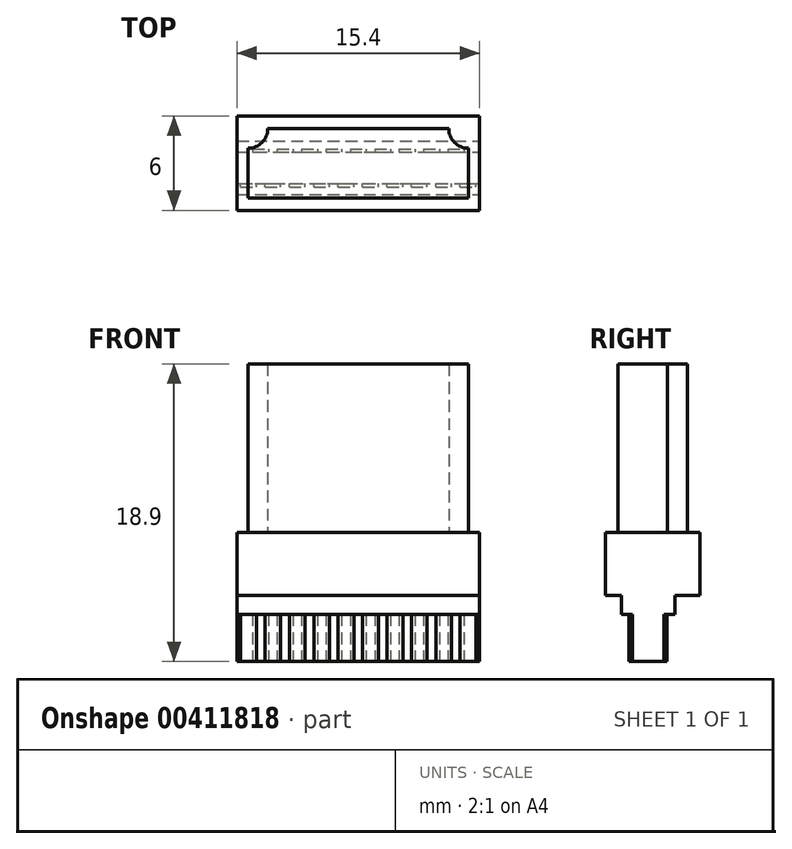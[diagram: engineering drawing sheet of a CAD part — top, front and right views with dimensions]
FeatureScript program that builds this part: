
annotation { "Feature Type Name" : "Feature", "Feature Type Description" : "" }
export const myFeature = defineFeature(function(context is Context, id is Id, definition is map)
    precondition{}
    {
        {
            var Q0;
            Q0=qCreatedBy(makeId("Top.planeOp"),FACE);
            var sketch = newSketch(context, id + "F0", { "sketchPlane" : qUnion([Q0])});
            skLineSegment(sketch, "E0.bottom", {"start": v(0, 0) * mm, "end": v(14, 0) * mm});
            skLineSegment(sketch, "E0.top", {"start": v(1.25, 4.4) * mm, "end": v(12.75, 4.4) * mm});
            skLineSegment(sketch, "E0.left", {"start": v(0, 0) * mm, "end": v(0, 3.15) * mm});
            skLineSegment(sketch, "E0.right", {"start": v(14, 0) * mm, "end": v(14, 3.15) * mm});
            skArc(sketch, "E1", {"start": v(0, 3.15) * mm, "mid": v(0.88, 3.52) * mm, "end": v(1.25, 4.4) * mm});
            skArc(sketch, "E2", {"start": v(12.75, 4.4) * mm, "mid": v(13.12, 3.52) * mm, "end": v(14, 3.15) * mm});
            skSolve(sketch);
        }
        {
            var Q0;
            Q0=makeQuery(id+"F0.imprint","IMPRINT",FACE,{"disambiguationData":[TD([[makeQuery(id+"F0.imprint","IMPRINT",EDGE,{"derivedFrom":sQuery(id+"F0.wireOp",EDGE,"E0.bottom")}),1.0]])]});
            extrude(context, id + "F1", {"entities" : qUnion([Q0]), "depth" : 10.7 * mm});
        }
        {
            var Q0;
            Q0=makeQuery(id+"F1.opExtrude","CAP_FACE",FACE,{"disambiguationData":[OSD([sQuery(id+"F0.wireOp",EDGE,"E0.bottom"),sQuery(id+"F0.wireOp",EDGE,"E0.top"),sQuery(id+"F0.wireOp",EDGE,"E0.left"),sQuery(id+"F0.wireOp",EDGE,"E0.right"),sQuery(id+"F0.wireOp",EDGE,"E1"),sQuery(id+"F0.wireOp",EDGE,"E2")])],"isStart":true});
            var sketch = newSketch(context, id + "F2", { "sketchPlane" : qUnion([Q0])});
            skLineSegment(sketch, "E3.bottom", {"start": v(-0.7, 0.8) * mm, "end": v(14.7, 0.8) * mm});
            skLineSegment(sketch, "E3.top", {"start": v(-0.7, -5.2) * mm, "end": v(14.7, -5.2) * mm});
            skLineSegment(sketch, "E3.left", {"start": v(-0.7, 0.8) * mm, "end": v(-0.7, -5.2) * mm});
            skLineSegment(sketch, "E3.right", {"start": v(14.7, 0.8) * mm, "end": v(14.7, -5.2) * mm});
            skSolve(sketch);
        }
        {
            var Q0;
            Q0=makeQuery(id+"F2.imprint","IMPRINT",FACE,{"disambiguationData":[TD([[makeQuery(id+"F2.imprint","IMPRINT",EDGE,{"derivedFrom":sQuery(id+"F2.wireOp",EDGE,"E3.bottom")}),-1.0]])]});
            var Q1;
            Q1=makeQuery(id+"F2.imprint","IMPRINT",FACE,{"disambiguationData":[TD([[makeQuery(id+"F2.imprint","IMPRINT",EDGE,{"derivedFrom":makeQuery(id+"F1.opExtrude","CAP_EDGE",EDGE,{"disambiguationData":[OSD([sQuery(id+"F0.wireOp",EDGE,"E0.bottom")])],"isStart":true})}),-1.0]])]});
            extrude(context, id + "F3", {"entities" : qUnion([Q0, Q1]), "depth" : 4 * mm});
        }
        {
            var Q0;
            Q0=makeQuery(id+"F3.opExtrude","CAP_FACE",FACE,{"disambiguationData":[OSD([sQuery(id+"F2.wireOp",EDGE,"E3.bottom"),sQuery(id+"F2.wireOp",EDGE,"E3.top"),sQuery(id+"F2.wireOp",EDGE,"E3.left"),sQuery(id+"F2.wireOp",EDGE,"E3.right")])],"isStart":false});
            var sketch = newSketch(context, id + "F4", { "sketchPlane" : qUnion([Q0])});
            skLineSegment(sketch, "E4.bottom", {"start": v(-0.7, -0.2) * mm, "end": v(14.7, -0.2) * mm});
            skLineSegment(sketch, "E4.top", {"start": v(-0.7, -3.6) * mm, "end": v(14.7, -3.6) * mm});
            skLineSegment(sketch, "E4.left", {"start": v(-0.7, -0.2) * mm, "end": v(-0.7, -3.6) * mm});
            skLineSegment(sketch, "E4.right", {"start": v(14.7, -0.2) * mm, "end": v(14.7, -3.6) * mm});
            skSolve(sketch);
        }
        {
            var Q0;
            Q0=makeQuery(id+"F4.imprint","IMPRINT",FACE,{"disambiguationData":[TD([[makeQuery(id+"F4.imprint","IMPRINT",EDGE,{"derivedFrom":sQuery(id+"F4.wireOp",EDGE,"E4.bottom")}),-1.0]])]});
            extrude(context, id + "F5", {"entities" : qUnion([Q0]), "operationType" : NewBodyOperationType.ADD, "depth" : 1.2 * mm});
        }
        {
            var Q0;
            Q0=makeQuery(id+"F5.opExtrude","CAP_FACE",FACE,{"disambiguationData":[OSD([sQuery(id+"F4.wireOp",EDGE,"E4.bottom"),sQuery(id+"F4.wireOp",EDGE,"E4.top"),sQuery(id+"F4.wireOp",EDGE,"E4.left"),sQuery(id+"F4.wireOp",EDGE,"E4.right")])],"isStart":false});
            var sketch = newSketch(context, id + "F6", { "sketchPlane" : qUnion([Q0])});
            skLineSegment(sketch, "E5.bottom", {"start": v(-0.7, -0.9) * mm, "end": v(14.7, -0.9) * mm});
            skLineSegment(sketch, "E5.top", {"start": v(-0.7, -2.9) * mm, "end": v(14.7, -2.9) * mm});
            skLineSegment(sketch, "E5.left", {"start": v(-0.7, -0.9) * mm, "end": v(-0.7, -2.9) * mm});
            skLineSegment(sketch, "E5.right", {"start": v(14.7, -0.9) * mm, "end": v(14.7, -2.9) * mm});
            skSolve(sketch);
        }
        {
            var Q0;
            Q0=makeQuery(id+"F6.imprint","IMPRINT",FACE,{"disambiguationData":[TD([[makeQuery(id+"F6.imprint","IMPRINT",EDGE,{"derivedFrom":sQuery(id+"F6.wireOp",EDGE,"E5.bottom")}),-1.0]])]});
            extrude(context, id + "F7", {"entities" : qUnion([Q0]), "operationType" : NewBodyOperationType.ADD, "depth" : 3 * mm});
        }
        {
            var Q0;
            Q0=makeQuery(id+"F7.opExtrude","SWEPT_FACE",FACE,{"disambiguationData":[OSD([sQuery(id+"F6.wireOp",EDGE,"E5.bottom")])]});
            var sketch = newSketch(context, id + "F8", { "sketchPlane" : qUnion([Q0])});
            skLineSegment(sketch, "E6.bottom", {"start": v(-0.47, -5.2) * mm, "end": v(0.52, -5.2) * mm});
            skLineSegment(sketch, "E6.top", {"start": v(-0.47, -8.2) * mm, "end": v(0.53, -8.2) * mm});
            skLineSegment(sketch, "E6.left", {"start": v(-0.48, -5.2) * mm, "end": v(-0.47, -8.2) * mm});
            skLineSegment(sketch, "E6.right", {"start": v(0.52, -5.2) * mm, "end": v(0.53, -8.2) * mm});
            skLineSegment(sketch, "E7.1.0.0", {"start": v(1.08, -5.2) * mm, "end": v(2.07, -5.2) * mm});
            skLineSegment(sketch, "E7.1.0.1", {"start": v(1.07, -5.2) * mm, "end": v(1.08, -8.2) * mm});
            skLineSegment(sketch, "E7.1.0.2", {"start": v(2.08, -5.2) * mm, "end": v(2.08, -8.2) * mm});
            skLineSegment(sketch, "E7.1.0.3", {"start": v(1.08, -8.2) * mm, "end": v(2.08, -8.2) * mm});
            skLineSegment(sketch, "E7.2.0.0", {"start": v(2.63, -5.2) * mm, "end": v(3.62, -5.2) * mm});
            skLineSegment(sketch, "E7.2.0.1", {"start": v(2.62, -5.2) * mm, "end": v(2.62, -8.2) * mm});
            skLineSegment(sketch, "E7.2.0.2", {"start": v(3.62, -5.2) * mm, "end": v(3.62, -8.2) * mm});
            skLineSegment(sketch, "E7.2.0.3", {"start": v(2.63, -8.2) * mm, "end": v(3.62, -8.2) * mm});
            skLineSegment(sketch, "E7.3.0.0", {"start": v(4.18, -5.2) * mm, "end": v(5.17, -5.2) * mm});
            skLineSegment(sketch, "E7.3.0.1", {"start": v(4.18, -5.2) * mm, "end": v(4.18, -8.2) * mm});
            skLineSegment(sketch, "E7.3.0.2", {"start": v(5.17, -5.2) * mm, "end": v(5.17, -8.2) * mm});
            skLineSegment(sketch, "E7.3.0.3", {"start": v(4.18, -8.2) * mm, "end": v(5.18, -8.2) * mm});
            skLineSegment(sketch, "E7.4.0.0", {"start": v(5.73, -5.2) * mm, "end": v(6.72, -5.2) * mm});
            skLineSegment(sketch, "E7.4.0.1", {"start": v(5.73, -5.2) * mm, "end": v(5.73, -8.2) * mm});
            skLineSegment(sketch, "E7.4.0.2", {"start": v(6.72, -5.2) * mm, "end": v(6.72, -8.2) * mm});
            skLineSegment(sketch, "E7.4.0.3", {"start": v(5.73, -8.2) * mm, "end": v(6.73, -8.2) * mm});
            skLineSegment(sketch, "E7.5.0.0", {"start": v(7.28, -5.2) * mm, "end": v(8.28, -5.2) * mm});
            skLineSegment(sketch, "E7.5.0.1", {"start": v(7.28, -5.2) * mm, "end": v(7.28, -8.2) * mm});
            skLineSegment(sketch, "E7.5.0.2", {"start": v(8.28, -5.2) * mm, "end": v(8.28, -8.2) * mm});
            skLineSegment(sketch, "E7.5.0.3", {"start": v(7.28, -8.2) * mm, "end": v(8.28, -8.2) * mm});
            skLineSegment(sketch, "E7.6.0.0", {"start": v(8.83, -5.2) * mm, "end": v(9.83, -5.2) * mm});
            skLineSegment(sketch, "E7.6.0.1", {"start": v(8.83, -5.2) * mm, "end": v(8.83, -8.2) * mm});
            skLineSegment(sketch, "E7.6.0.2", {"start": v(9.83, -5.2) * mm, "end": v(9.83, -8.2) * mm});
            skLineSegment(sketch, "E7.6.0.3", {"start": v(8.83, -8.2) * mm, "end": v(9.83, -8.2) * mm});
            skLineSegment(sketch, "E7.7.0.0", {"start": v(10.38, -5.2) * mm, "end": v(11.38, -5.2) * mm});
            skLineSegment(sketch, "E7.7.0.1", {"start": v(10.38, -5.2) * mm, "end": v(10.38, -8.2) * mm});
            skLineSegment(sketch, "E7.7.0.2", {"start": v(11.38, -5.2) * mm, "end": v(11.38, -8.2) * mm});
            skLineSegment(sketch, "E7.7.0.3", {"start": v(10.38, -8.2) * mm, "end": v(11.38, -8.2) * mm});
            skLineSegment(sketch, "E7.8.0.0", {"start": v(11.93, -5.2) * mm, "end": v(12.93, -5.2) * mm});
            skLineSegment(sketch, "E7.8.0.1", {"start": v(11.93, -5.2) * mm, "end": v(11.93, -8.2) * mm});
            skLineSegment(sketch, "E7.8.0.2", {"start": v(12.93, -5.2) * mm, "end": v(12.93, -8.2) * mm});
            skLineSegment(sketch, "E7.8.0.3", {"start": v(11.93, -8.2) * mm, "end": v(12.93, -8.2) * mm});
            skLineSegment(sketch, "E7.9.0.0", {"start": v(13.48, -5.2) * mm, "end": v(14.47, -5.2) * mm});
            skLineSegment(sketch, "E7.9.0.1", {"start": v(13.48, -5.2) * mm, "end": v(13.48, -8.2) * mm});
            skLineSegment(sketch, "E7.9.0.2", {"start": v(14.47, -5.2) * mm, "end": v(14.47, -8.2) * mm});
            skLineSegment(sketch, "E7.9.0.3", {"start": v(13.48, -8.2) * mm, "end": v(14.47, -8.2) * mm});
            skLineSegment(sketch, "E7.direction1", {"start": v(-0.47, -5.2) * mm, "end": v(1.08, -5.2) * mm, "construction": true});
            skSolve(sketch);
        }
        {
            var Q0;
            Q0=makeQuery(id+"F8.imprint","IMPRINT",FACE,{"disambiguationData":[TD([[makeQuery(id+"F8.imprint","IMPRINT",EDGE,{"derivedFrom":sQuery(id+"F8.wireOp",EDGE,"E6.bottom")}),-1.0]])]});
            var Q1;
            Q1=makeQuery(id+"F8.imprint","IMPRINT",FACE,{"disambiguationData":[TD([[makeQuery(id+"F8.imprint","IMPRINT",EDGE,{"derivedFrom":sQuery(id+"F8.wireOp",EDGE,"E7.1.0.0")}),-1.0]])]});
            var Q2;
            Q2=makeQuery(id+"F8.imprint","IMPRINT",FACE,{"disambiguationData":[TD([[makeQuery(id+"F8.imprint","IMPRINT",EDGE,{"derivedFrom":sQuery(id+"F8.wireOp",EDGE,"E7.2.0.0")}),-1.0]])]});
            var Q3;
            Q3=makeQuery(id+"F8.imprint","IMPRINT",FACE,{"disambiguationData":[TD([[makeQuery(id+"F8.imprint","IMPRINT",EDGE,{"derivedFrom":sQuery(id+"F8.wireOp",EDGE,"E7.3.0.0")}),-1.0]])]});
            var Q4;
            Q4=makeQuery(id+"F8.imprint","IMPRINT",FACE,{"disambiguationData":[TD([[makeQuery(id+"F8.imprint","IMPRINT",EDGE,{"derivedFrom":sQuery(id+"F8.wireOp",EDGE,"E7.4.0.0")}),-1.0]])]});
            var Q5;
            Q5=makeQuery(id+"F8.imprint","IMPRINT",FACE,{"disambiguationData":[TD([[makeQuery(id+"F8.imprint","IMPRINT",EDGE,{"derivedFrom":sQuery(id+"F8.wireOp",EDGE,"E7.5.0.0")}),-1.0]])]});
            var Q6;
            Q6=makeQuery(id+"F8.imprint","IMPRINT",FACE,{"disambiguationData":[TD([[makeQuery(id+"F8.imprint","IMPRINT",EDGE,{"derivedFrom":sQuery(id+"F8.wireOp",EDGE,"E7.6.0.0")}),-1.0]])]});
            var Q7;
            Q7=makeQuery(id+"F8.imprint","IMPRINT",FACE,{"disambiguationData":[TD([[makeQuery(id+"F8.imprint","IMPRINT",EDGE,{"derivedFrom":sQuery(id+"F8.wireOp",EDGE,"E7.7.0.0")}),-1.0]])]});
            var Q8;
            Q8=makeQuery(id+"F8.imprint","IMPRINT",FACE,{"disambiguationData":[TD([[makeQuery(id+"F8.imprint","IMPRINT",EDGE,{"derivedFrom":sQuery(id+"F8.wireOp",EDGE,"E7.8.0.0")}),-1.0]])]});
            var Q9;
            Q9=makeQuery(id+"F8.imprint","IMPRINT",FACE,{"disambiguationData":[TD([[makeQuery(id+"F8.imprint","IMPRINT",EDGE,{"derivedFrom":sQuery(id+"F8.wireOp",EDGE,"E7.9.0.0")}),-1.0]])]});
            extrude(context, id + "F9", {"entities" : qUnion([Q0, Q1, Q2, Q3, Q4, Q5, Q6, Q7, Q8, Q9]), "depth" : 0.2 * mm});
        }
        {
            var Q0;
            Q0=makeQuery(id+"F7.opExtrude","SWEPT_FACE",FACE,{"disambiguationData":[OSD([sQuery(id+"F6.wireOp",EDGE,"E5.top")])]});
            var sketch = newSketch(context, id + "F10", { "sketchPlane" : qUnion([Q0])});
            skLineSegment(sketch, "E8.bottom", {"start": v(-13.7, -5.2) * mm, "end": v(-12.7, -5.2) * mm});
            skLineSegment(sketch, "E8.top", {"start": v(-13.7, -8.2) * mm, "end": v(-12.7, -8.2) * mm});
            skLineSegment(sketch, "E8.left", {"start": v(-13.7, -5.2) * mm, "end": v(-13.7, -8.2) * mm});
            skLineSegment(sketch, "E8.right", {"start": v(-12.7, -5.2) * mm, "end": v(-12.7, -8.2) * mm});
            skLineSegment(sketch, "E9.1.0.0", {"start": v(-12.15, -5.2) * mm, "end": v(-11.15, -5.2) * mm});
            skLineSegment(sketch, "E9.1.0.1", {"start": v(-12.15, -5.2) * mm, "end": v(-12.15, -8.2) * mm});
            skLineSegment(sketch, "E9.1.0.2", {"start": v(-11.15, -5.2) * mm, "end": v(-11.15, -8.2) * mm});
            skLineSegment(sketch, "E9.1.0.3", {"start": v(-12.15, -8.2) * mm, "end": v(-11.15, -8.2) * mm});
            skLineSegment(sketch, "E9.2.0.0", {"start": v(-10.6, -5.2) * mm, "end": v(-9.6, -5.2) * mm});
            skLineSegment(sketch, "E9.2.0.1", {"start": v(-10.6, -5.2) * mm, "end": v(-10.6, -8.2) * mm});
            skLineSegment(sketch, "E9.2.0.2", {"start": v(-9.6, -5.2) * mm, "end": v(-9.6, -8.2) * mm});
            skLineSegment(sketch, "E9.2.0.3", {"start": v(-10.6, -8.2) * mm, "end": v(-9.6, -8.2) * mm});
            skLineSegment(sketch, "E9.3.0.0", {"start": v(-9.05, -5.2) * mm, "end": v(-8.05, -5.2) * mm});
            skLineSegment(sketch, "E9.3.0.1", {"start": v(-9.05, -5.2) * mm, "end": v(-9.05, -8.2) * mm});
            skLineSegment(sketch, "E9.3.0.2", {"start": v(-8.05, -5.2) * mm, "end": v(-8.05, -8.2) * mm});
            skLineSegment(sketch, "E9.3.0.3", {"start": v(-9.05, -8.2) * mm, "end": v(-8.05, -8.2) * mm});
            skLineSegment(sketch, "E9.4.0.0", {"start": v(-7.5, -5.2) * mm, "end": v(-6.5, -5.2) * mm});
            skLineSegment(sketch, "E9.4.0.1", {"start": v(-7.5, -5.2) * mm, "end": v(-7.5, -8.2) * mm});
            skLineSegment(sketch, "E9.4.0.2", {"start": v(-6.5, -5.2) * mm, "end": v(-6.5, -8.2) * mm});
            skLineSegment(sketch, "E9.4.0.3", {"start": v(-7.5, -8.2) * mm, "end": v(-6.5, -8.2) * mm});
            skLineSegment(sketch, "E9.5.0.0", {"start": v(-5.95, -5.2) * mm, "end": v(-4.95, -5.2) * mm});
            skLineSegment(sketch, "E9.5.0.1", {"start": v(-5.95, -5.2) * mm, "end": v(-5.95, -8.2) * mm});
            skLineSegment(sketch, "E9.5.0.2", {"start": v(-4.95, -5.2) * mm, "end": v(-4.95, -8.2) * mm});
            skLineSegment(sketch, "E9.5.0.3", {"start": v(-5.95, -8.2) * mm, "end": v(-4.95, -8.2) * mm});
            skLineSegment(sketch, "E9.6.0.0", {"start": v(-4.4, -5.2) * mm, "end": v(-3.4, -5.2) * mm});
            skLineSegment(sketch, "E9.6.0.1", {"start": v(-4.4, -5.2) * mm, "end": v(-4.4, -8.2) * mm});
            skLineSegment(sketch, "E9.6.0.2", {"start": v(-3.4, -5.2) * mm, "end": v(-3.4, -8.2) * mm});
            skLineSegment(sketch, "E9.6.0.3", {"start": v(-4.4, -8.2) * mm, "end": v(-3.4, -8.2) * mm});
            skLineSegment(sketch, "E9.7.0.0", {"start": v(-2.85, -5.2) * mm, "end": v(-1.85, -5.2) * mm});
            skLineSegment(sketch, "E9.7.0.1", {"start": v(-2.85, -5.2) * mm, "end": v(-2.85, -8.2) * mm});
            skLineSegment(sketch, "E9.7.0.2", {"start": v(-1.85, -5.2) * mm, "end": v(-1.85, -8.2) * mm});
            skLineSegment(sketch, "E9.7.0.3", {"start": v(-2.85, -8.2) * mm, "end": v(-1.85, -8.2) * mm});
            skLineSegment(sketch, "E9.8.0.0", {"start": v(-1.3, -5.2) * mm, "end": v(-0.3, -5.2) * mm});
            skLineSegment(sketch, "E9.8.0.1", {"start": v(-1.3, -5.2) * mm, "end": v(-1.3, -8.2) * mm});
            skLineSegment(sketch, "E9.8.0.2", {"start": v(-0.3, -5.2) * mm, "end": v(-0.3, -8.2) * mm});
            skLineSegment(sketch, "E9.8.0.3", {"start": v(-1.3, -8.2) * mm, "end": v(-0.3, -8.2) * mm});
            skLineSegment(sketch, "E9.direction1", {"start": v(-13.7, -5.2) * mm, "end": v(-12.15, -5.2) * mm, "construction": true});
            skSolve(sketch);
        }
        {
            var Q0;
            Q0=makeQuery(id+"F10.imprint","IMPRINT",FACE,{"disambiguationData":[TD([[makeQuery(id+"F10.imprint","IMPRINT",EDGE,{"derivedFrom":sQuery(id+"F10.wireOp",EDGE,"E8.bottom")}),1.0]])]});
            var Q1;
            Q1=makeQuery(id+"F10.imprint","IMPRINT",FACE,{"disambiguationData":[TD([[makeQuery(id+"F10.imprint","IMPRINT",EDGE,{"derivedFrom":sQuery(id+"F10.wireOp",EDGE,"E9.1.0.0")}),1.0]])]});
            var Q2;
            Q2=makeQuery(id+"F10.imprint","IMPRINT",FACE,{"disambiguationData":[TD([[makeQuery(id+"F10.imprint","IMPRINT",EDGE,{"derivedFrom":sQuery(id+"F10.wireOp",EDGE,"E9.2.0.0")}),1.0]])]});
            var Q3;
            Q3=makeQuery(id+"F10.imprint","IMPRINT",FACE,{"disambiguationData":[TD([[makeQuery(id+"F10.imprint","IMPRINT",EDGE,{"derivedFrom":sQuery(id+"F10.wireOp",EDGE,"E9.3.0.0")}),1.0]])]});
            var Q4;
            Q4=makeQuery(id+"F10.imprint","IMPRINT",FACE,{"disambiguationData":[TD([[makeQuery(id+"F10.imprint","IMPRINT",EDGE,{"derivedFrom":sQuery(id+"F10.wireOp",EDGE,"E9.4.0.0")}),1.0]])]});
            var Q5;
            Q5=makeQuery(id+"F10.imprint","IMPRINT",FACE,{"disambiguationData":[TD([[makeQuery(id+"F10.imprint","IMPRINT",EDGE,{"derivedFrom":sQuery(id+"F10.wireOp",EDGE,"E9.5.0.0")}),1.0]])]});
            var Q6;
            Q6=makeQuery(id+"F10.imprint","IMPRINT",FACE,{"disambiguationData":[TD([[makeQuery(id+"F10.imprint","IMPRINT",EDGE,{"derivedFrom":sQuery(id+"F10.wireOp",EDGE,"E9.6.0.0")}),1.0]])]});
            var Q7;
            Q7=makeQuery(id+"F10.imprint","IMPRINT",FACE,{"disambiguationData":[TD([[makeQuery(id+"F10.imprint","IMPRINT",EDGE,{"derivedFrom":sQuery(id+"F10.wireOp",EDGE,"E9.7.0.0")}),1.0]])]});
            var Q8;
            Q8=makeQuery(id+"F10.imprint","IMPRINT",FACE,{"disambiguationData":[TD([[makeQuery(id+"F10.imprint","IMPRINT",EDGE,{"derivedFrom":sQuery(id+"F10.wireOp",EDGE,"E9.8.0.0")}),1.0]])]});
            extrude(context, id + "F11", {"entities" : qUnion([Q0, Q1, Q2, Q3, Q4, Q5, Q6, Q7, Q8]), "depth" : 0.2 * mm});
        }
    });
